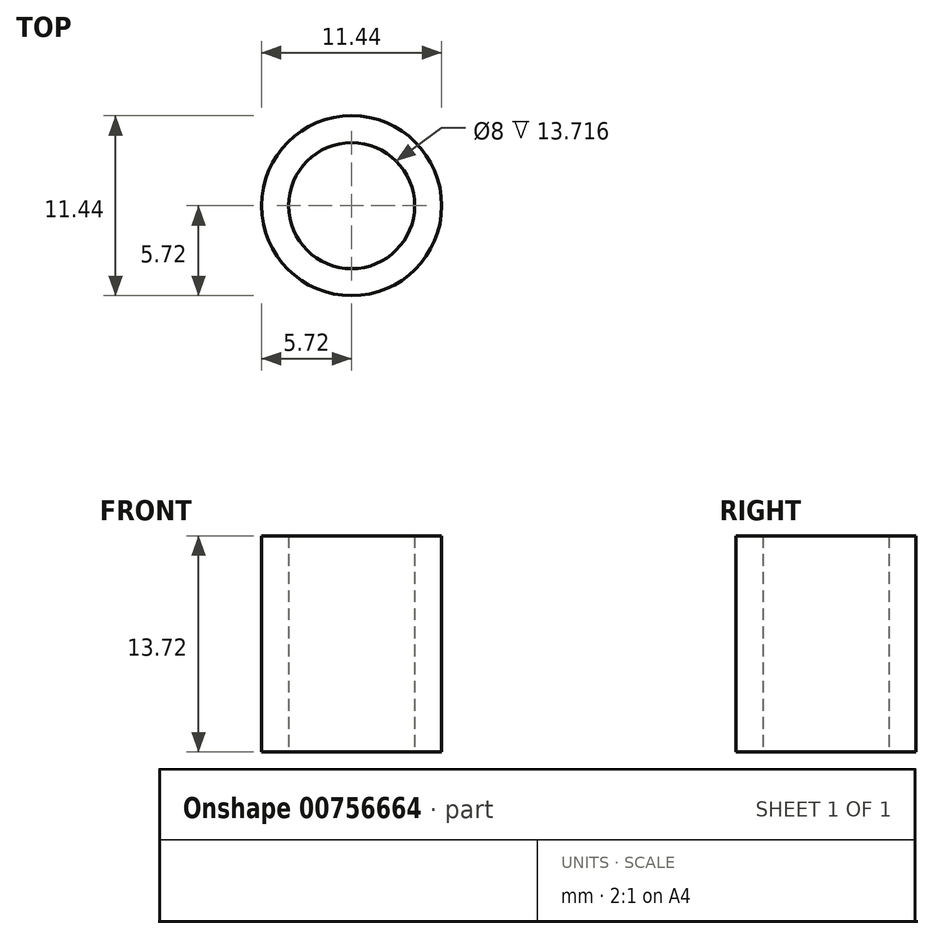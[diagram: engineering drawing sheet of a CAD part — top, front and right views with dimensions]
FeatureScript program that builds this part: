
annotation { "Feature Type Name" : "Feature", "Feature Type Description" : "" }
export const myFeature = defineFeature(function(context is Context, id is Id, definition is map)
    precondition{}
    {
        {
            var Q0;
            Q0=qCreatedBy(makeId("Top.planeOp"),FACE);
            var sketch = newSketch(context, id + "F0", { "sketchPlane" : qUnion([Q0])});
            skCircle(sketch, "E0", {"center": v(0, 0) * mm, "radius": 5.72 * mm});
            skCircle(sketch, "E1", {"center": v(0, 0) * mm, "radius": 4 * mm});
            skSolve(sketch);
        }
        {
            var Q0;
            Q0=makeQuery(id+"F0.imprint","IMPRINT",FACE,{"disambiguationData":[TD([[makeQuery(id+"F0.imprint","IMPRINT",EDGE,{"derivedFrom":sQuery(id+"F0.wireOp",EDGE,"E0")}),1.0]])]});
            extrude(context, id + "F1", {"entities" : qUnion([Q0]), "depth" : 13.72 * mm, "offsetDistance" : 25.4 * mm});
        }
    });
